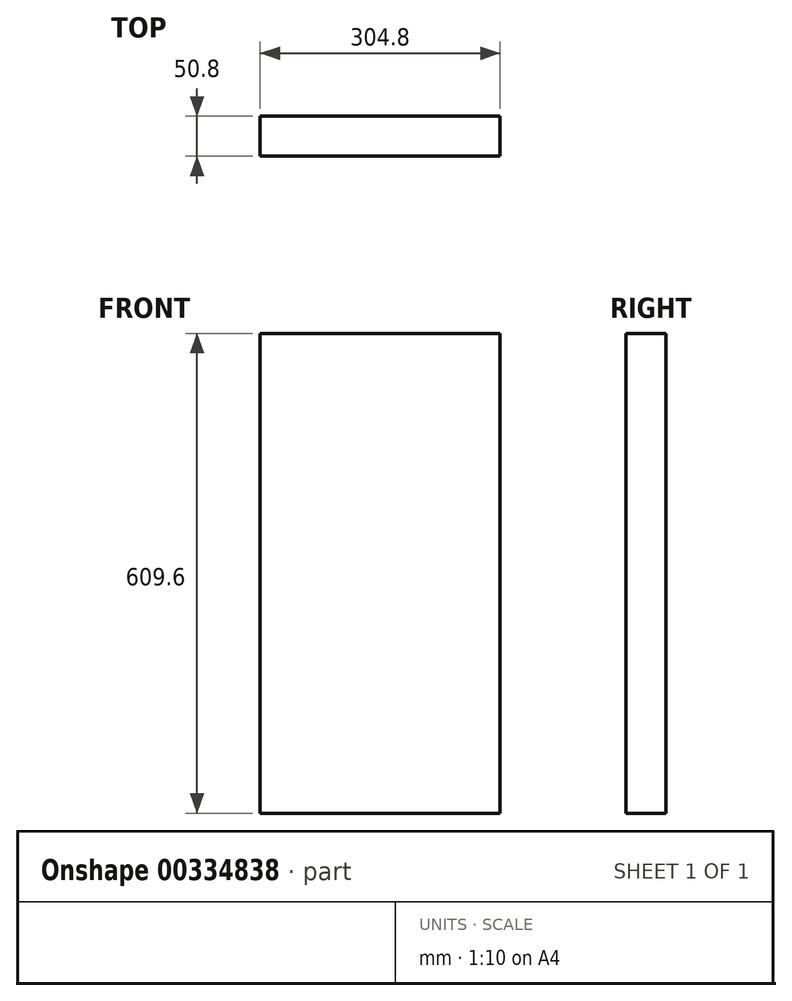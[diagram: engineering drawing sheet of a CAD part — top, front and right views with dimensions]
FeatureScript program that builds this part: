
annotation { "Feature Type Name" : "Feature", "Feature Type Description" : "" }
export const myFeature = defineFeature(function(context is Context, id is Id, definition is map)
    precondition{}
    {
        {
            var Q0;
            Q0=qCreatedBy(makeId("Front.planeOp"),FACE);
            var sketch = newSketch(context, id + "F0", { "sketchPlane" : qUnion([Q0])});
            skLineSegment(sketch, "E0.bottom", {"start": v(-152.4, 304.8) * mm, "end": v(152.4, 304.8) * mm});
            skLineSegment(sketch, "E0.top", {"start": v(-152.4, -304.8) * mm, "end": v(152.4, -304.8) * mm});
            skLineSegment(sketch, "E0.left", {"start": v(-152.4, 304.8) * mm, "end": v(-152.4, -304.8) * mm});
            skLineSegment(sketch, "E0.right", {"start": v(152.4, 304.8) * mm, "end": v(152.4, -304.8) * mm});
            skPoint(sketch, "E0.middle", {"position": v(0, 0) * mm});
            skSolve(sketch);
        }
        {
            var Q0;
            Q0=makeQuery(id+"F0.imprint","IMPRINT",FACE,{"disambiguationData":[TD([[makeQuery(id+"F0.imprint","IMPRINT",EDGE,{"derivedFrom":sQuery(id+"F0.wireOp",EDGE,"E0.bottom")}),-1.0]])]});
            extrude(context, id + "F1", {"entities" : qUnion([Q0]), "depth" : 50.8 * mm});
        }
    });
